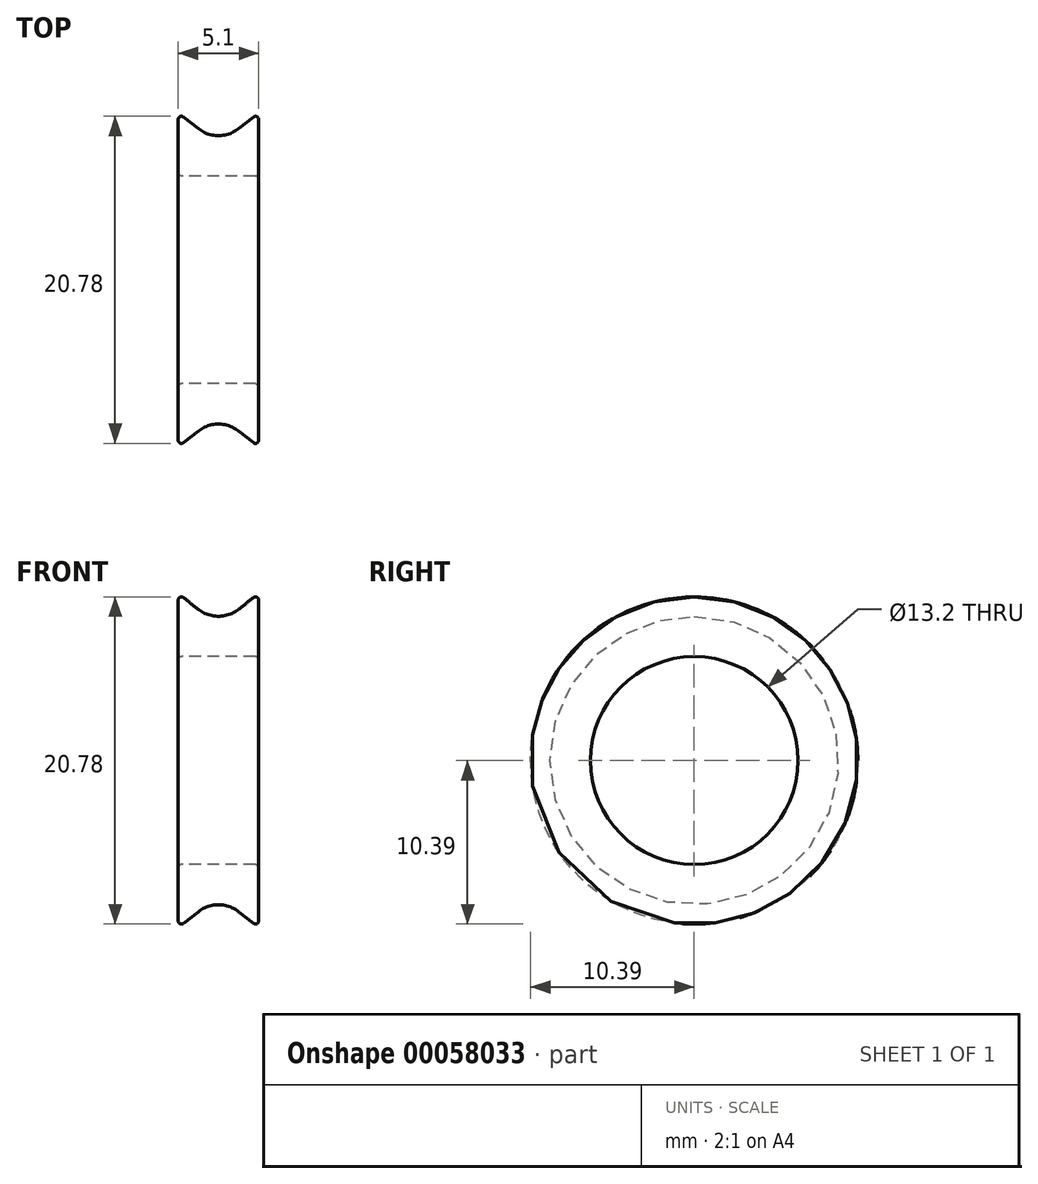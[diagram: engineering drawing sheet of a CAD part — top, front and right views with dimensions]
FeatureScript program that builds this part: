
annotation { "Feature Type Name" : "Feature", "Feature Type Description" : "" }
export const myFeature = defineFeature(function(context is Context, id is Id, definition is map)
    precondition{}
    {
        {
            var Q0;
            Q0=qCreatedBy(makeId("Front.planeOp"),FACE);
            var sketch = newSketch(context, id + "F0", { "sketchPlane" : qUnion([Q0])});
            skLineSegment(sketch, "E0", {"start": v(-2.55, 0) * mm, "end": v(2.55, 0) * mm, "construction": true});
            skLineSegment(sketch, "E1", {"start": v(-2.35, 6.6) * mm, "end": v(2.35, 6.6) * mm});
            skLineSegment(sketch, "E2", {"start": v(-2.55, 6.8) * mm, "end": v(-2.55, 10.19) * mm});
            skLineSegment(sketch, "E3", {"start": v(-2.55, 10.6) * mm, "end": v(0, 8.6) * mm, "construction": true});
            skLineSegment(sketch, "E4", {"start": v(0, 8.6) * mm, "end": v(2.55, 10.6) * mm, "construction": true});
            skLineSegment(sketch, "E5", {"start": v(2.55, 10.19) * mm, "end": v(2.55, 6.8) * mm});
            skLineSegment(sketch, "E6", {"start": v(0, 8.6) * mm, "end": v(0, 6.6) * mm, "construction": true});
            skLineSegment(sketch, "E7", {"start": v(-1.28, 9.6) * mm, "end": v(-2.23, 10.35) * mm});
            skLineSegment(sketch, "E8", {"start": v(1.28, 9.6) * mm, "end": v(2.23, 10.35) * mm});
            skArc(sketch, "E9", {"start": v(-1.28, 9.6) * mm, "mid": v(0, 9.16) * mm, "end": v(1.28, 9.6) * mm});
            skPoint(sketch, "E10.visualSharp", {"position": v(2.55, 10.6) * mm});
            skArc(sketch, "E10.filletArc", {"start": v(2.55, 10.19) * mm, "mid": v(2.44, 10.37) * mm, "end": v(2.23, 10.35) * mm});
            skPoint(sketch, "E11.visualSharp", {"position": v(-2.55, 10.6) * mm});
            skArc(sketch, "E11.filletArc", {"start": v(-2.23, 10.35) * mm, "mid": v(-2.44, 10.37) * mm, "end": v(-2.55, 10.19) * mm});
            skPoint(sketch, "E12.visualSharp", {"position": v(2.55, 6.6) * mm});
            skArc(sketch, "E12.filletArc", {"start": v(2.35, 6.6) * mm, "mid": v(2.5, 6.66) * mm, "end": v(2.55, 6.8) * mm});
            skPoint(sketch, "E13.visualSharp", {"position": v(-2.55, 6.6) * mm});
            skArc(sketch, "E13.filletArc", {"start": v(-2.55, 6.8) * mm, "mid": v(-2.5, 6.66) * mm, "end": v(-2.35, 6.6) * mm});
            skSolve(sketch);
        }
        {
            var Q0;
            Q0 = qSketchRegion(id + "F0", true);
            var Q1;
            Q1=sQuery(id+"F0.wireOp",EDGE,"E0");
            revolve(context, id + "F1", {"entities" : qUnion([Q0]), "axis" : qUnion([Q1]), "revolveType" : RevolveType.FULL});
        }
    });
